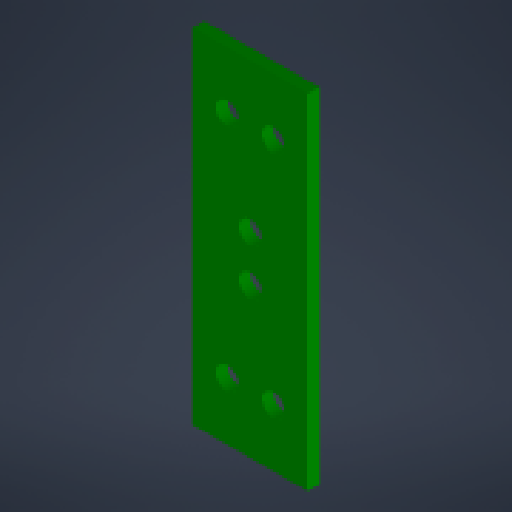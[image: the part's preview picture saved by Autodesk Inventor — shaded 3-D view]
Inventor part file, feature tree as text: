
AUTODESK INVENTOR PART (.ipt)
format: ipt  version: 2024 (Build 280153000, 153)  size: 182,784 bytes
history: native  units: mm
features: other x6, reference x6, extrude x2, sketch x2
ambient origin geometry x8: Origin, YZ Plane, XZ Plane, XY Plane, X Axis, Y Axis, Z Axis, Center Point
bodies: Body1 (feature_tree)
feature tree (16):
  other  "Твердое тело1"
  extrude  "Выдавливание1"  Depth=60.0mm
  extrude  "Выдавливание2"  Depth=20.0mm
  sketch  "Эскиз2"
  sketch  "Эскиз3"
  reference  "Ссылка1"
  reference  "Ссылка2"
  reference  "Ссылка3"
  reference  "Ссылка4"
  reference  "Ссылка5"
  reference  "Ссылка6"
  parser-record x1  (decoder bookkeeping rows leaked as tree rows — omitted from the tree; the rows remain in map.json)
  other  "base_assembly.iam"
  other  "side_section:1"
  other  "main axis:1"
  other  "side_section:2"
note: 1 file-system path scrubbed to <path> (originals preserved in map.json)
